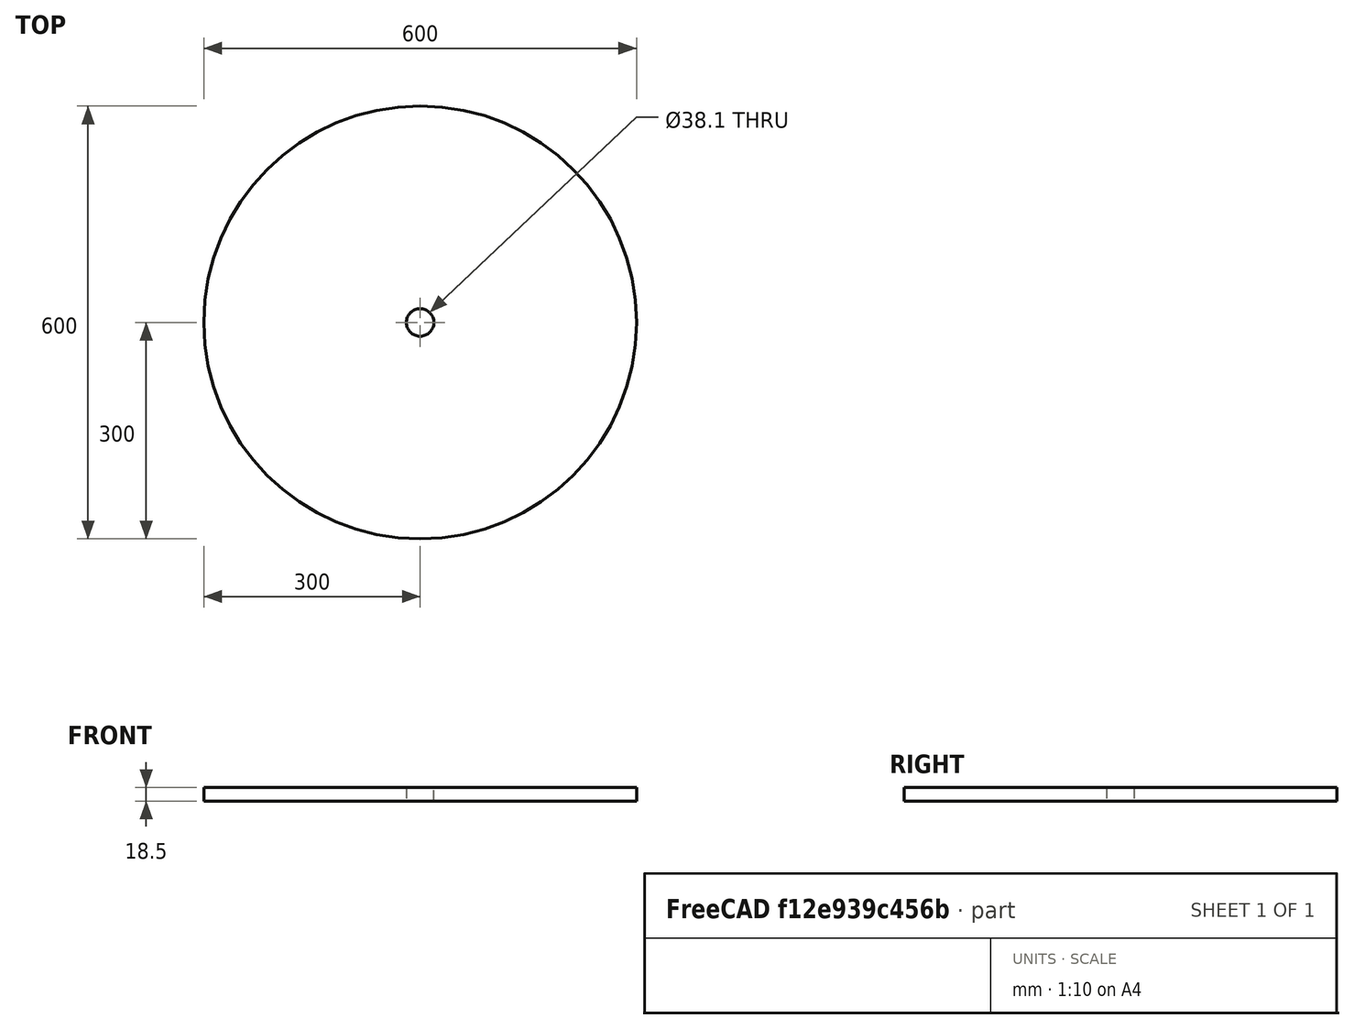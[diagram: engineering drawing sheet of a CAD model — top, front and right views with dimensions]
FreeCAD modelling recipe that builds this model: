
FCSTD DOCUMENT  (FreeCAD 0.20R29410 (Git))
Label: MainWheel
License: All rights reserved
LicenseURL: http://en.wikipedia.org/wiki/All_rights_reserved
objects: Sketcher::SketchObject×1, PartDesign::CoordinateSystem×1, PartDesign::Pad×1, PartDesign::Body×1
note: 5 computed .brp shape members not serialized (recipe doc carries the construction recipe); baked Part::Feature solids carry a one-line shape summary decoded from their .brp
EXTERNAL_REF file=Params.FCStd obj=Spreadsheet

FEATURE [Sketcher::SketchObject] Sketch001
  FullyConstrained = true
  MapMode = 5
  Support = -> [XY_Plane]
  sketch-geometry (2):
    g0: Circle CenterX=0 CenterY=0 CenterZ=0 NormalX=0 NormalY=0 NormalZ=1 AngleXU=0 Radius=19.05
    g1: Circle CenterX=0 CenterY=0 CenterZ=0 NormalX=0 NormalY=0 NormalZ=1 AngleXU=0 Radius=300
  constraints (4):
    c: Coincident(g0,g-1)
    c: Diameter(g0) = 38.1
    c: Coincident(g1,g0)
    c: Diameter(g1) = 600
FEATURE [PartDesign::CoordinateSystem] LCS_1
  AttacherType = Attacher::AttachEngine3D
  MapMode = 2
  Support = -> [XY_Plane]
FEATURE [PartDesign::Pad] Pad
  Direction = (0,0,1)
  Length = 18.5
  Length2 = 10
  Profile = -> Sketch001
  ReferenceAxis = -> Sketch001 [N_Axis]
  Type = 0
  expr: Length = <<Params>>#<<Params>>.PlywoodThickness
FEATURE [PartDesign::Body] Body
  Group = -> [Sketch001,LCS_1,Pad]
  Origin = -> Origin
  Tip = -> Pad
